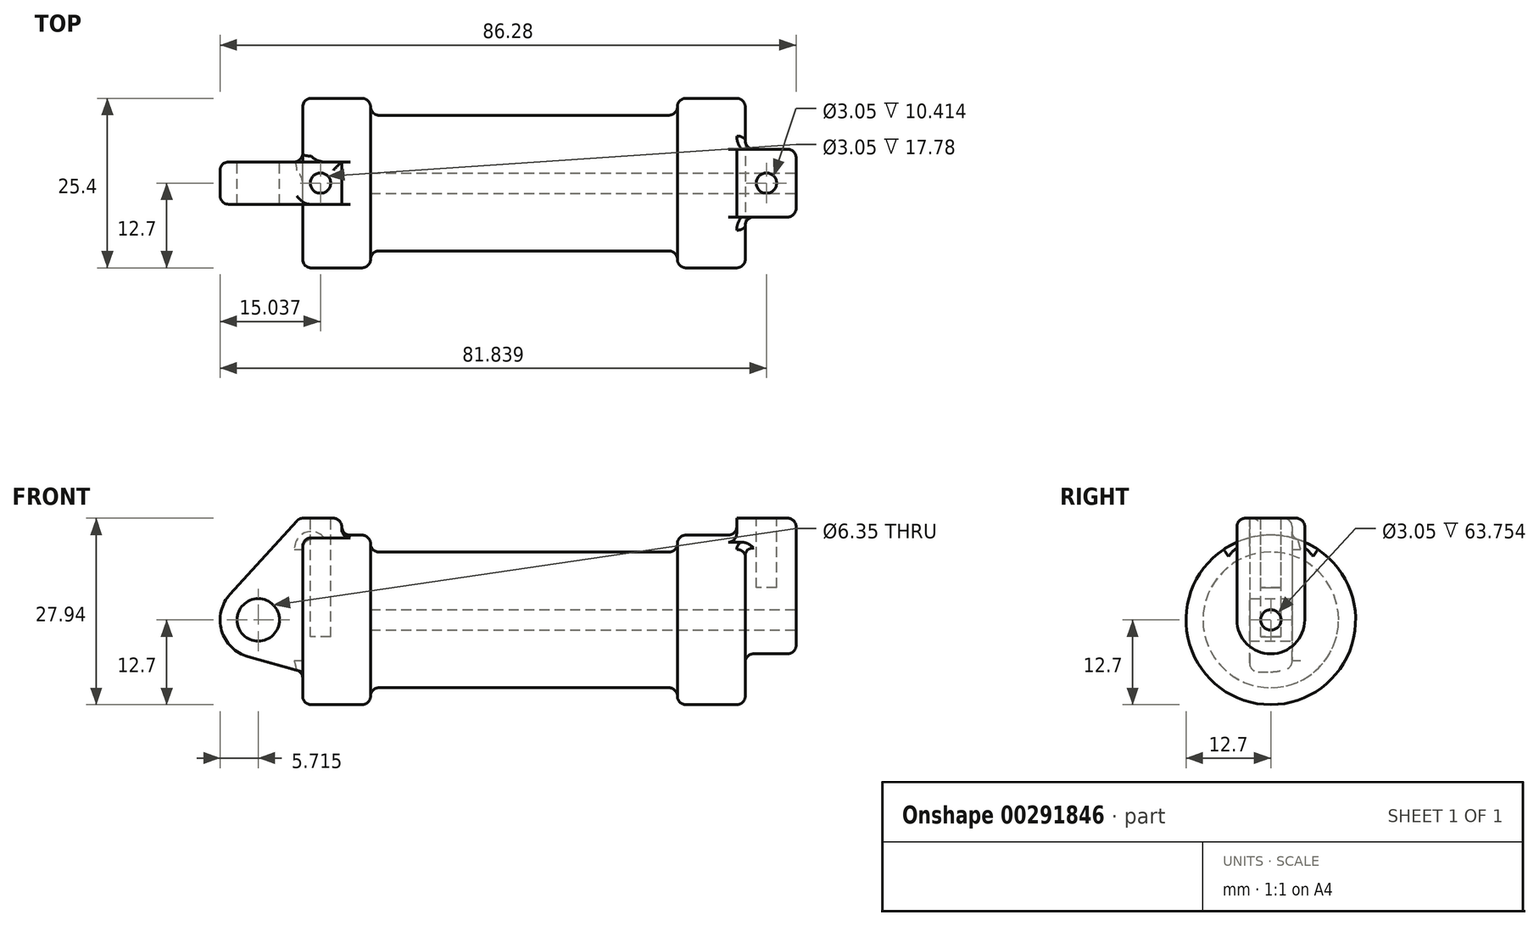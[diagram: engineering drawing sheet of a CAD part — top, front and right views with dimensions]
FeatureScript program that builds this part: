
annotation { "Feature Type Name" : "Feature", "Feature Type Description" : "" }
export const myFeature = defineFeature(function(context is Context, id is Id, definition is map)
    precondition{}
    {
        {
            var Q0;
            Q0=qCreatedBy(makeId("Front.planeOp"),FACE);
            var sketch = newSketch(context, id + "F0", { "sketchPlane" : qUnion([Q0])});
            skLineSegment(sketch, "E0", {"start": v(0, 0) * mm, "end": v(0, 12.7) * mm});
            skLineSegment(sketch, "E1", {"start": v(0, 12.7) * mm, "end": v(10.16, 12.7) * mm});
            skLineSegment(sketch, "E2", {"start": v(10.16, 12.7) * mm, "end": v(10.16, 10.16) * mm});
            skLineSegment(sketch, "E3", {"start": v(10.16, 10.16) * mm, "end": v(56.13, 10.16) * mm});
            skLineSegment(sketch, "E4", {"start": v(56.13, 10.16) * mm, "end": v(56.13, 12.7) * mm});
            skLineSegment(sketch, "E5", {"start": v(56.13, 12.7) * mm, "end": v(66.3, 12.7) * mm});
            skLineSegment(sketch, "E6", {"start": v(66.3, 12.7) * mm, "end": v(66.3, 0) * mm});
            skLineSegment(sketch, "E7", {"start": v(66.3, 0) * mm, "end": v(0, 0) * mm});
            skLineSegment(sketch, "E8", {"start": v(5.84, 15.24) * mm, "end": v(-0.5, 15.24) * mm});
            skLineSegment(sketch, "E9", {"start": v(-0.5, 15.24) * mm, "end": v(-10.88, 3.85) * mm});
            skLineSegment(sketch, "E10", {"start": v(0, 0) * mm, "end": v(-6.65, 0) * mm});
            skCircle(sketch, "E11", {"center": v(-6.65, 0) * mm, "radius": 5.72 * mm});
            skCircle(sketch, "E12", {"center": v(-6.65, 0) * mm, "radius": 3.18 * mm});
            skLineSegment(sketch, "E13", {"start": v(5.84, 15.24) * mm, "end": v(5.84, -9.4) * mm});
            skLineSegment(sketch, "E14", {"start": v(5.84, -9.4) * mm, "end": v(-8.18, -5.5) * mm});
            skSolve(sketch);
        }
        {
            var Q0;
            {var subQ0=sQuery(id+"F0.wireOp",EDGE,"E2");Q0=makeQuery(id+"F0.imprint","IMPRINT",FACE,{"disambiguationData":[TD([[makeQuery(id+"F0.imprint","IMPRINT",EDGE,{"derivedFrom":subQ0}),-1.0]])]});}
            var Q1;
            {var subQ0=sQuery(id+"F0.wireOp",EDGE,"E0");Q1=makeQuery(id+"F0.imprint","IMPRINT",FACE,{"disambiguationData":[TD([[makeQuery(id+"F0.imprint","IMPRINT",EDGE,{"derivedFrom":subQ0}),-1.0]])]});}
            var Q2;
            Q2=sQuery(id+"F0.wireOp",EDGE,"E7");
            revolve(context, id + "F1", {"entities" : qUnion([Q0, Q1]), "axis" : qUnion([Q2]), "revolveType" : RevolveType.FULL});
        }
        {
            var Q0;
            {var subQ1=sQuery(id+"F0.wireOp",EDGE,"E0");Q0=makeQuery(id+"F0.imprint","IMPRINT",FACE,{"disambiguationData":[TD([[makeQuery(id+"F0.imprint","IMPRINT",EDGE,{"derivedFrom":subQ1}),1.0]])]});}
            var Q1;
            Q1=makeQuery(id+"F0.imprint","IMPRINT",FACE,{"disambiguationData":[TD([[makeQuery(id+"F0.imprint","IMPRINT",EDGE,{"derivedFrom":sQuery(id+"F0.wireOp",EDGE,"E12")}),-1.0]])]});
            var Q2;
            {var subQ0=sQuery(id+"F0.wireOp",EDGE,"E0");Q2=makeQuery(id+"F0.imprint","IMPRINT",FACE,{"disambiguationData":[TD([[makeQuery(id+"F0.imprint","IMPRINT",EDGE,{"derivedFrom":subQ0}),-1.0]])]});}
            var Q3;
            {var subQ0=sQuery(id+"F0.wireOp",EDGE,"E14");Q3=makeQuery(id+"F0.imprint","IMPRINT",FACE,{"disambiguationData":[TD([[makeQuery(id+"F0.imprint","IMPRINT",EDGE,{"derivedFrom":subQ0}),-1.0]])]});}
            extrude(context, id + "F2", {"entities" : qUnion([Q0, Q1, Q2, Q3]), "operationType" : NewBodyOperationType.ADD, "endBound" : BoundingType.SYMMETRIC, "depth" : 6.35 * mm});
        }
        {
            var Q0;
            Q0=makeQuery(id+"F1.opRevolve","SWEPT_FACE",FACE,{"disambiguationData":[OSD([sQuery(id+"F0.wireOp",EDGE,"E6")])]});
            var sketch = newSketch(context, id + "F3", { "sketchPlane" : qUnion([Q0])});
            skCircle(sketch, "E15", {"center": v(0, 0) * mm, "radius": 1.52 * mm});
            skCircle(sketch, "E16", {"center": v(0, 0) * mm, "radius": 5.08 * mm});
            skLineSegment(sketch, "E17", {"start": v(-5.08, 0) * mm, "end": v(-5.08, 15.24) * mm});
            skLineSegment(sketch, "E18", {"start": v(-5.08, 15.24) * mm, "end": v(5.08, 15.24) * mm});
            skLineSegment(sketch, "E19", {"start": v(5.08, 15.24) * mm, "end": v(5.08, 0) * mm});
            skLineSegment(sketch, "E20", {"start": v(-12.7, 0) * mm, "end": v(12.7, 0) * mm, "construction": true});
            skSolve(sketch);
        }
        {
            var Q0;
            Q0=makeQuery(id+"F3.imprint","IMPRINT",FACE,{"disambiguationData":[TD([[makeQuery(id+"F3.imprint","IMPRINT",EDGE,{"derivedFrom":sQuery(id+"F3.wireOp",EDGE,"E15")}),1.0]])]});
            var Q1;
            Q1=makeQuery(id+"F1.opRevolve","SWEPT_FACE",FACE,{"disambiguationData":[OSD([sQuery(id+"F0.wireOp",EDGE,"E2")])]});
            extrude(context, id + "F4", {"entities" : qUnion([Q0]), "operationType" : NewBodyOperationType.REMOVE, "endBound" : BoundingType.UP_TO_SURFACE, "oppositeDirection" : true, "endBoundEntityFace" : qUnion([Q1]), "depth" : 25.4 * mm});
        }
        {
            var Q0;
            Q0=makeQuery(id+"F3.imprint","IMPRINT",FACE,{"disambiguationData":[TD([[makeQuery(id+"F3.imprint","IMPRINT",EDGE,{"derivedFrom":sQuery(id+"F3.wireOp",EDGE,"E15")}),-1.0]])]});
            var Q1;
            {var subQ0=sQuery(id+"F3.wireOp",EDGE,"E17");var subQ1=sQuery(id+"F3.wireOp",EDGE,"E16");var subQ2=makeQuery(id+"F3.imprint","INTERSECT",VERTEX,{"derivedFrom":[subQ1,subQ0]});Q1=makeQuery(id+"F3.imprint","IMPRINT",FACE,{"disambiguationData":[TD([[makeQuery(id+"F3.imprint","IMPRINT",EDGE,{"disambiguationData":[TD([[subQ2,1.0]])],"derivedFrom":subQ1}),-1.0]])]});}
            var Q2;
            {var subQ0=sQuery(id+"F3.wireOp",EDGE,"E18");Q2=makeQuery(id+"F3.imprint","IMPRINT",FACE,{"disambiguationData":[TD([[makeQuery(id+"F3.imprint","IMPRINT",EDGE,{"derivedFrom":subQ0}),-1.0]])]});}
            extrude(context, id + "F5", {"entities" : qUnion([Q0, Q1, Q2]), "operationType" : NewBodyOperationType.ADD, "depth" : 7.62 * mm, "hasSecondDirection" : true, "secondDirectionOppositeDirection" : true, "secondDirectionDepth" : 1.27 * mm});
        }
        {
            var Q0;
            Q0=makeQuery(id+"F2.opExtrude","SWEPT_FACE",FACE,{"disambiguationData":[OSD([sQuery(id+"F0.wireOp",EDGE,"E8")])]});
            var sketch = newSketch(context, id + "F6", { "sketchPlane" : qUnion([Q0])});
            skLineSegment(sketch, "E21", {"start": v(2.67, 3.18) * mm, "end": v(2.67, -3.18) * mm, "construction": true});
            skCircle(sketch, "E22", {"center": v(2.67, 0) * mm, "radius": 1.52 * mm});
            skSolve(sketch);
        }
        {
            var Q0;
            Q0=makeQuery(id+"F5.opExtrude","SWEPT_FACE",FACE,{"disambiguationData":[OSD([sQuery(id+"F3.wireOp",EDGE,"E18")])]});
            var sketch = newSketch(context, id + "F7", { "sketchPlane" : qUnion([Q0])});
            skLineSegment(sketch, "E23", {"start": v(69.47, 5.08) * mm, "end": v(69.47, -5.08) * mm, "construction": true});
            skCircle(sketch, "E24", {"center": v(69.47, 0) * mm, "radius": 1.52 * mm});
            skSolve(sketch);
        }
        {
            var Q0;
            Q0=makeQuery(id+"F7.imprint","IMPRINT",FACE,{"disambiguationData":[TD([[makeQuery(id+"F7.imprint","IMPRINT",EDGE,{"derivedFrom":sQuery(id+"F7.wireOp",EDGE,"E24")}),1.0]])]});
            extrude(context, id + "F8", {"entities" : qUnion([Q0]), "operationType" : NewBodyOperationType.REMOVE, "oppositeDirection" : true, "depth" : 10.4 * mm});
        }
        {
            var Q0;
            Q0=makeQuery(id+"F6.imprint","IMPRINT",FACE,{"disambiguationData":[TD([[makeQuery(id+"F6.imprint","IMPRINT",EDGE,{"derivedFrom":sQuery(id+"F6.wireOp",EDGE,"E22")}),1.0]])]});
            extrude(context, id + "F9", {"entities" : qUnion([Q0]), "operationType" : NewBodyOperationType.REMOVE, "oppositeDirection" : true, "depth" : 17.78 * mm});
        }
        {
            var Q0;
            Q0=makeQuery(id+"F1.opRevolve","SWEPT_EDGE",EDGE,{"disambiguationData":[OSD([sQuery(id+"F0.wireOp",EDGE,"E0"),sQuery(id+"F0.wireOp",EDGE,"E1")])]});
            var Q1;
            Q1=makeQuery(id+"F2.boolean.opBoolean","INTERSECT",EDGE,{"derivedFrom":[makeQuery(id+"F1.opRevolve","SWEPT_FACE",FACE,{"disambiguationData":[OSD([sQuery(id+"F0.wireOp",EDGE,"E0")])]}),makeQuery(id+"F2.opExtrude","CAP_FACE",FACE,{"disambiguationData":[OSD([sQuery(id+"F0.wireOp",EDGE,"E8"),sQuery(id+"F0.wireOp",EDGE,"E9"),sQuery(id+"F0.wireOp",EDGE,"E11"),sQuery(id+"F0.wireOp",EDGE,"E12"),sQuery(id+"F0.wireOp",EDGE,"E13"),sQuery(id+"F0.wireOp",EDGE,"E14")])],"isStart":true})]});
            var Q2;
            Q2=makeQuery(id+"F2.opExtrude","CAP_EDGE",EDGE,{"disambiguationData":[OSD([sQuery(id+"F0.wireOp",EDGE,"E8")])],"isStart":true});
            var Q3;
            Q3=makeQuery(id+"F2.opExtrude","CAP_EDGE",EDGE,{"disambiguationData":[OSD([sQuery(id+"F0.wireOp",EDGE,"E9")])],"isStart":true});
            var Q4;
            Q4=makeQuery(id+"F2.opExtrude","SWEPT_EDGE",EDGE,{"disambiguationData":[OSD([sQuery(id+"F0.wireOp",EDGE,"E8"),sQuery(id+"F0.wireOp",EDGE,"E13")])]});
            var Q5;
            Q5=makeQuery(id+"F2.opExtrude","SWEPT_EDGE",EDGE,{"disambiguationData":[OSD([sQuery(id+"F0.wireOp",EDGE,"E8"),sQuery(id+"F0.wireOp",EDGE,"E9")])]});
            var Q6;
            Q6=makeQuery(id+"F2.opExtrude","CAP_EDGE",EDGE,{"disambiguationData":[OSD([sQuery(id+"F0.wireOp",EDGE,"E11")])],"isStart":false});
            var Q7;
            Q7=makeQuery(id+"F1.opRevolve","SWEPT_EDGE",EDGE,{"disambiguationData":[OSD([sQuery(id+"F0.wireOp",EDGE,"E1"),sQuery(id+"F0.wireOp",EDGE,"E2")])]});
            var Q8;
            Q8=makeQuery(id+"F2.boolean.opBoolean","INTERSECT",EDGE,{"derivedFrom":[makeQuery(id+"F1.opRevolve","SWEPT_FACE",FACE,{"disambiguationData":[OSD([sQuery(id+"F0.wireOp",EDGE,"E1")])]}),makeQuery(id+"F2.opExtrude","SWEPT_FACE",FACE,{"disambiguationData":[OSD([sQuery(id+"F0.wireOp",EDGE,"E13")])]})]});
            fillet(context, id + "F10", {"entities" : qUnion([Q0, Q1, Q2, Q3, Q4, Q5, Q6, Q7, Q8]), "radius" : 1.27 * mm, "tangentPropagation" : true, "allowEdgeOverflow" : false});
        }
        {
            var Q0;
            Q0=makeQuery(id+"F5.boolean.opBoolean","INTERSECT",EDGE,{"derivedFrom":[makeQuery(id+"F1.opRevolve","SWEPT_FACE",FACE,{"disambiguationData":[OSD([sQuery(id+"F0.wireOp",EDGE,"E6")])]}),makeQuery(id+"F5.opExtrude","SWEPT_FACE",FACE,{"disambiguationData":[OSD([sQuery(id+"F3.wireOp",EDGE,"E16")])]})]});
            var Q1;
            Q1=makeQuery(id+"F5.opExtrude","CAP_EDGE",EDGE,{"disambiguationData":[OSD([sQuery(id+"F3.wireOp",EDGE,"E16")])],"isStart":false});
            var Q2;
            Q2=makeQuery(id+"F5.opExtrude","CAP_EDGE",EDGE,{"disambiguationData":[OSD([sQuery(id+"F3.wireOp",EDGE,"E18")])],"isStart":false});
            var Q3;
            Q3=makeQuery(id+"F5.boolean.opBoolean","INTERSECT",EDGE,{"derivedFrom":[makeQuery(id+"F1.opRevolve","SWEPT_FACE",FACE,{"disambiguationData":[OSD([sQuery(id+"F0.wireOp",EDGE,"E5")])]}),makeQuery(id+"F5.opExtrude","CAP_FACE",FACE,{"disambiguationData":[OSD([sQuery(id+"F3.wireOp",EDGE,"E15"),sQuery(id+"F3.wireOp",EDGE,"E16"),sQuery(id+"F3.wireOp",EDGE,"E17"),sQuery(id+"F3.wireOp",EDGE,"E18"),sQuery(id+"F3.wireOp",EDGE,"E19")])],"isStart":true})]});
            var Q4;
            Q4=makeQuery(id+"F5.opExtrude","SWEPT_EDGE",EDGE,{"disambiguationData":[OSD([sQuery(id+"F3.wireOp",EDGE,"E18"),sQuery(id+"F3.wireOp",EDGE,"E19")])]});
            var Q5;
            Q5=makeQuery(id+"F5.opExtrude","SWEPT_EDGE",EDGE,{"disambiguationData":[OSD([sQuery(id+"F3.wireOp",EDGE,"E17"),sQuery(id+"F3.wireOp",EDGE,"E18")])]});
            var Q6;
            Q6=makeQuery(id+"F1.opRevolve","SWEPT_EDGE",EDGE,{"disambiguationData":[OSD([sQuery(id+"F0.wireOp",EDGE,"E4"),sQuery(id+"F0.wireOp",EDGE,"E5")])]});
            fillet(context, id + "F11", {"entities" : qUnion([Q0, Q1, Q2, Q3, Q4, Q5, Q6]), "radius" : 1.27 * mm, "tangentPropagation" : true, "allowEdgeOverflow" : false});
        }
        {
            var Q0;
            Q0=makeQuery(id+"F1.opRevolve","SWEPT_EDGE",EDGE,{"disambiguationData":[OSD([sQuery(id+"F0.wireOp",EDGE,"E5"),sQuery(id+"F0.wireOp",EDGE,"E6")])]});
            var Q1;
            Q1=makeQuery(id+"F1.opRevolve","SWEPT_EDGE",EDGE,{"disambiguationData":[OSD([sQuery(id+"F0.wireOp",EDGE,"E3"),sQuery(id+"F0.wireOp",EDGE,"E4")])]});
            var Q2;
            Q2=makeQuery(id+"F1.opRevolve","SWEPT_EDGE",EDGE,{"disambiguationData":[OSD([sQuery(id+"F0.wireOp",EDGE,"E2"),sQuery(id+"F0.wireOp",EDGE,"E3")])]});
            fillet(context, id + "F12", {"entities" : qUnion([Q0, Q1, Q2]), "radius" : 1.27 * mm, "tangentPropagation" : true, "allowEdgeOverflow" : false});
        }
    });
